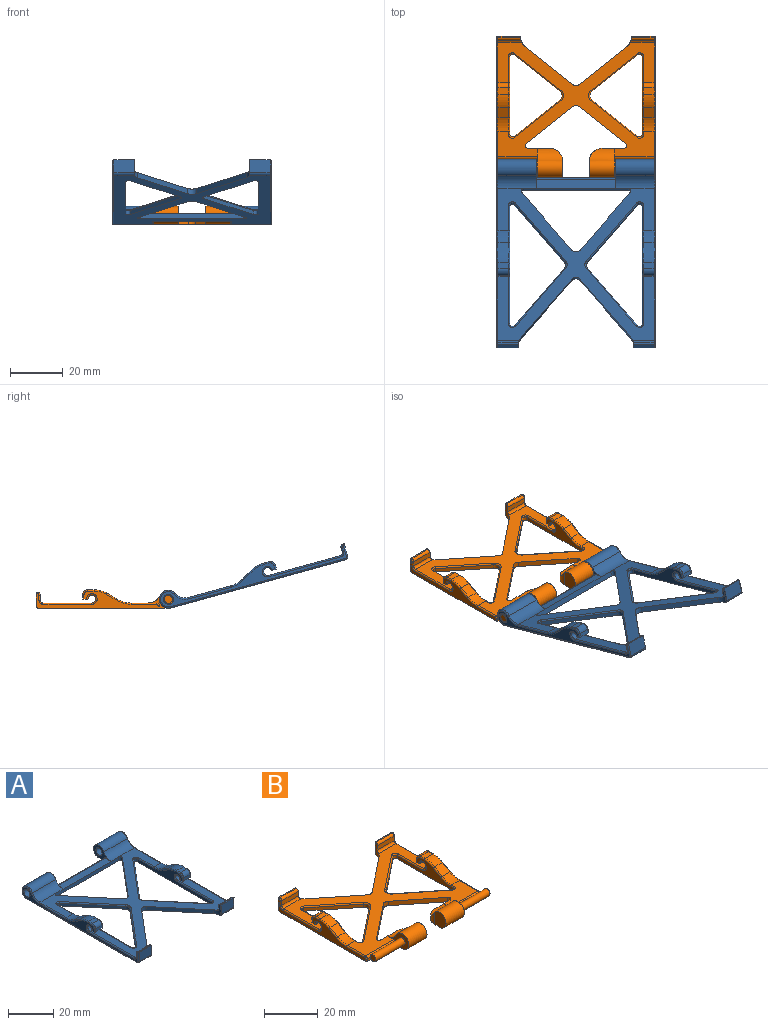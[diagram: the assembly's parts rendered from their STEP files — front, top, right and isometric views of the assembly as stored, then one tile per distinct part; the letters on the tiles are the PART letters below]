
ASSEMBLY  parts=2 mates=1
PART A: 132 faces, bbox 60x73.4x8.1 mm
  f0: plane 68.6x59mm, normal (0,0,-1), area 1652.7mm2, adj f4,f10,f14,f16,f19,f23,f25,f33
  f1: plane 7.77x5mm, normal (0,-1,0), area 38.8mm2, adj f3,f4,f55,f113
  f2: plane 7.83x2mm, normal (0,1,0), area 15.7mm2, adj f5,f6,f57,f107
  f3: plane 7.77x0.5mm, normal (0,0,1), area 3.9mm2, adj f1,f5,f55,f111
  f4: cylinder r=1mm len=7.78mm, axis (1,0,0), area 12.2mm2, adj f0,f1,f55,f57,f112
  f5: cylinder r=1mm len=7.83mm, axis (1,0,0), area 12.2mm2, adj f2,f3,f55,f57,f109
  f6: cylinder r=1mm len=8.11mm, axis (-1,0,0), area 12.4mm2, adj f2,f8,f57,f105
  f7: plane 30x3.49mm, normal (0,0,1), area 104.7mm2, adj f16,f18,f25,f48
  f8: plane 59.51x59mm, normal (0,0,1), area 1041.3mm2, adj f6,f17,f21,f26,f27,f34,f43,f44
  f9: plane 72x6mm, normal (-1,0,0), area 126.8mm2, adj f15,f32,f96,f97,f98,f99,f100,f101
  f10: plane 30x1mm, normal (0,1,0), area 30mm2, adj f0,f16,f18,f25
  f11: plane 7.83x2mm, normal (0,1,0), area 15.7mm2, adj f20,f21,f56,f125
  f12: plane 7.77x5mm, normal (0,-1,0), area 38.8mm2, adj f13,f19,f54,f131
  f13: plane 7.77x0.5mm, normal (0,0,1), area 3.9mm2, adj f12,f20,f54,f129
  f14: cylinder r=3.4mm len=14.5mm, axis (-1,0,0), area 210.5mm2, adj f0,f16,f17,f108
  f15: cylinder r=1.9mm len=15mm, axis (-1,0,0), area 179.1mm2, adj f9,f16
  f16: plane 10.99x6.8mm, normal (1,0,0), area 29.9mm2, adj f0,f7,f10,f14,f15,f17,f18
  f17: cylinder r=5mm len=14.5mm, axis (-1,0,0), area 81.8mm2, adj f8,f14,f16,f48,f106
  f18: cylinder r=1mm len=30mm, axis (1,0,0), area 47.1mm2, adj f7,f10,f16,f25
  f19: cylinder r=1mm len=7.78mm, axis (1,0,0), area 12.2mm2, adj f0,f12,f54,f56,f130
  f20: cylinder r=1mm len=7.83mm, axis (1,0,0), area 12.2mm2, adj f11,f13,f54,f56,f127
  f21: cylinder r=1mm len=8.11mm, axis (-1,0,0), area 12.4mm2, adj f8,f11,f56,f123
  f22: plane 72x6mm, normal (1,0,0), area 126.8mm2, adj f24,f39,f114,f115,f116,f117,f118,f119
  f23: cylinder r=3.4mm len=14.5mm, axis (1,0,0), area 210.5mm2, adj f0,f25,f26,f126
  f24: cylinder r=1.9mm len=15mm, axis (1,0,0), area 179.1mm2, adj f22,f25
  f25: plane 10.99x6.8mm, normal (-1,0,0), area 29.9mm2, adj f0,f7,f10,f18,f23,f24,f26
  f26: cylinder r=5mm len=14.5mm, axis (1,0,0), area 81.8mm2, adj f8,f23,f25,f48,f124
  f27: cylinder r=1.5mm len=4mm, axis (-1,0,0), area 28.3mm2, adj f8,f32,f82,f101
  f28: plane 4.02x4mm, normal (0,0.5,0.87), area 18.6mm2, adj f52,f53,f91,f100
  f29: plane 4x2.32mm, normal (0,0,1), area 9.3mm2, adj f30,f53,f93,f98
  f30: cylinder r=2mm len=4mm, axis (-1,0,0), area 12.6mm2, adj f29,f31,f94,f97
  f31: plane 4x1.5mm, normal (0,-1,0), area 6mm2, adj f30,f32,f95,f96
  f32: plane 5x2mm, normal (0,0,-1), area 9.8mm2, adj f9,f27,f31,f33,f82,f95,f96,f101
  f33: plane 46.25x6.5mm, normal (1,0,0), area 107.1mm2, adj f0,f32,f66,f67,f82,f83,f89,f90
  f34: cylinder r=1.5mm len=4mm, axis (1,0,0), area 28.3mm2, adj f8,f39,f68,f119
  f35: plane 4.02x4mm, normal (0,0.5,0.87), area 18.6mm2, adj f50,f51,f77,f118
  f36: plane 4x2.32mm, normal (0,0,1), area 9.3mm2, adj f37,f51,f79,f116
  f37: cylinder r=2mm len=4mm, axis (1,0,0), area 12.6mm2, adj f36,f38,f80,f115
  f38: plane 4x1.5mm, normal (0,-1,0), area 6mm2, adj f37,f39,f81,f114
  f39: plane 5x2mm, normal (0,0,-1), area 9.8mm2, adj f22,f34,f38,f40,f68,f81,f114,f119
  f40: plane 46.25x6.5mm, normal (-1,0,0), area 107.1mm2, adj f0,f39,f64,f65,f68,f69,f75,f76
  f41: plane 22.48x18.89mm, normal (-0.77,0.64,0), area 44mm2, adj f0,f61,f67,f85
  f42: plane 22.48x18.89mm, normal (-0.77,-0.64,0), area 44mm2, adj f0,f61,f66,f87
  f43: plane 22.65x19.03mm, normal (-0.77,-0.64,0), area 59.2mm2, adj f0,f8,f56,f58
  f44: plane 22.65x19.03mm, normal (0.77,-0.64,0), area 59.2mm2, adj f0,f8,f57,f58
  f45: plane 22.48x18.89mm, normal (0.77,-0.64,0), area 44mm2, adj f0,f60,f64,f73
  f46: plane 22.48x18.89mm, normal (0.77,0.64,0), area 44mm2, adj f0,f60,f65,f71
  f47: plane 22.4x18.82mm, normal (0.77,0.64,0), area 58.5mm2, adj f0,f8,f59,f63
  f48: plane 39.18x2mm, normal (0,-1,0), area 78.4mm2, adj f0,f7,f17,f26,f62,f63
  f49: plane 22.4x18.82mm, normal (-0.77,0.64,0), area 58.5mm2, adj f0,f8,f59,f62
  f50: cylinder r=10mm len=5mm, axis (-1,0,0), area 20.9mm2, adj f8,f35,f76,f120
  f51: cylinder r=10mm len=5mm, axis (1,0,0), area 20.9mm2, adj f35,f36,f78,f117
  f52: cylinder r=10mm len=5mm, axis (1,0,0), area 20.9mm2, adj f8,f28,f90,f102
  f53: cylinder r=10mm len=5mm, axis (-1,0,0), area 20.9mm2, adj f28,f29,f92,f99
  f54: plane 5.95x0.68mm, normal (-1,0,0), area 3.9mm2, adj f12,f13,f19,f20,f56
  f55: plane 5.95x0.68mm, normal (1,0,0), area 3.9mm2, adj f1,f3,f4,f5,f57
  f56: cylinder r=5mm len=5.98mm, axis (0,0,1), area 10.3mm2, adj f0,f8,f11,f19,f20,f21,f43,f54
  f57: cylinder r=5mm len=5.98mm, axis (0,0,-1), area 10.3mm2, adj f0,f2,f4,f5,f6,f8,f44,f55
  f58: cylinder r=2mm len=3.06mm, axis (0,0,-1), area 7mm2, adj f0,f8,f43,f44
  f59: cylinder r=2mm len=3.06mm, axis (0,0,1), area 7mm2, adj f0,f8,f47,f49
  f60: cylinder r=2mm len=2.57mm, axis (0,0,-1), area 4.2mm2, adj f0,f45,f46,f72
  f61: cylinder r=2mm len=2.57mm, axis (0,0,-1), area 4.2mm2, adj f0,f41,f42,f86
  f62: cylinder r=1mm len=2mm, axis (0,0,1), area 4.5mm2, adj f0,f8,f48,f49
  f63: cylinder r=1mm len=2mm, axis (0,0,-1), area 4.5mm2, adj f0,f8,f47,f48
  f64: cylinder r=1mm len=1.77mm, axis (0,0,1), area 3.7mm2, adj f0,f40,f45,f74
  f65: cylinder r=1mm len=1.77mm, axis (0,0,1), area 3.7mm2, adj f0,f40,f46,f70
  f66: cylinder r=1mm len=1.77mm, axis (0,0,-1), area 3.7mm2, adj f0,f33,f42,f88
  f67: cylinder r=1mm len=1.77mm, axis (0,0,-1), area 3.7mm2, adj f0,f33,f41,f84
  f68: torus R=2mm, axis (1,0,0), area 6.2mm2, adj f34,f39,f40,f69
  f69: cylinder r=0.5mm len=21.57mm, axis (0,1,0), area 16.9mm2, adj f8,f40,f68,f70
  f70: torus R=1.5mm, axis (0,0,1), area 2.3mm2, adj f8,f65,f69,f71
  f71: cylinder r=0.5mm len=22.8mm, axis (-0.64,0.77,0), area 23.1mm2, adj f8,f46,f70,f72
  f72: torus R=2.5mm, axis (0,0,1), area 2.4mm2, adj f8,f60,f71,f73
  f73: cylinder r=0.5mm len=22.8mm, axis (0.64,0.77,0), area 23.1mm2, adj f8,f45,f72,f74
  f74: torus R=1.5mm, axis (0,0,1), area 2.3mm2, adj f8,f64,f73,f75
  f75: cylinder r=0.5mm len=9.84mm, axis (0,1,0), area 7.7mm2, adj f8,f40,f74,f76
  f76: torus R=10.5mm, axis (1,0,0), area 4.2mm2, adj f40,f50,f75,f77
  f77: cylinder r=0.5mm len=4.27mm, axis (0,0.87,-0.5), area 3.6mm2, adj f35,f40,f76,f78
  f78: torus R=9.5mm, axis (1,0,0), area 4mm2, adj f40,f51,f77,f79
  f79: cylinder r=0.5mm len=2.32mm, axis (0,1,0), area 1.8mm2, adj f36,f40,f78,f80
  f80: torus R=1.5mm, axis (1,0,0), area 2.2mm2, adj f37,f40,f79,f81
  f81: cylinder r=0.5mm len=1.5mm, axis (0,0,1), area 1.2mm2, adj f38,f39,f40,f80
  f82: torus R=2mm, axis (-1,0,0), area 6.2mm2, adj f27,f32,f33,f83
  f83: cylinder r=0.5mm len=21.57mm, axis (0,-1,0), area 16.9mm2, adj f8,f33,f82,f84
  f84: torus R=1.5mm, axis (0,0,1), area 2.3mm2, adj f8,f67,f83,f85
  f85: cylinder r=0.5mm len=22.8mm, axis (-0.64,-0.77,0), area 23.1mm2, adj f8,f41,f84,f86
  f86: torus R=2.5mm, axis (0,0,1), area 2.4mm2, adj f8,f61,f85,f87
  f87: cylinder r=0.5mm len=22.8mm, axis (0.64,-0.77,0), area 23.1mm2, adj f8,f42,f86,f88
  f88: torus R=1.5mm, axis (0,0,1), area 2.3mm2, adj f8,f66,f87,f89
  f89: cylinder r=0.5mm len=9.84mm, axis (0,-1,0), area 7.7mm2, adj f8,f33,f88,f90
  f90: torus R=10.5mm, axis (-1,0,0), area 4.2mm2, adj f33,f52,f89,f91
  f91: cylinder r=0.5mm len=4.27mm, axis (0,0.87,-0.5), area 3.6mm2, adj f28,f33,f90,f92
  f92: torus R=9.5mm, axis (-1,0,0), area 4mm2, adj f33,f53,f91,f93
  f93: cylinder r=0.5mm len=2.32mm, axis (0,1,0), area 1.8mm2, adj f29,f33,f92,f94
  f94: torus R=1.5mm, axis (-1,0,0), area 2.2mm2, adj f30,f33,f93,f95
  f95: cylinder r=0.5mm len=1.5mm, axis (0,0,1), area 1.2mm2, adj f31,f32,f33,f94
  f96: cylinder r=0.5mm len=1.5mm, axis (0,0,1), area 1.2mm2, adj f9,f31,f32,f97
  f97: torus R=1.5mm, axis (1,0,0), area 2.2mm2, adj f9,f30,f96,f98
  f98: cylinder r=0.5mm len=2.32mm, axis (0,1,0), area 1.8mm2, adj f9,f29,f97,f99
  f99: torus R=9.5mm, axis (1,0,0), area 4mm2, adj f9,f53,f98,f100
  f100: cylinder r=0.5mm len=4.27mm, axis (0,0.87,-0.5), area 3.6mm2, adj f9,f28,f99,f102
  f101: torus R=2mm, axis (1,0,0), area 6.2mm2, adj f9,f27,f32,f103
  f102: torus R=10.5mm, axis (1,0,0), area 4.2mm2, adj f9,f52,f100,f104
  f103: cylinder r=0.5mm len=28.2mm, axis (0,1,0), area 22.1mm2, adj f8,f9,f101,f105
  f104: cylinder r=0.5mm len=16.47mm, axis (0,1,0), area 12.9mm2, adj f8,f9,f102,f106
  f105: torus R=1.5mm, axis (1,0,0), area 1.5mm2, adj f6,f9,f103,f107
  f106: torus R=5.5mm, axis (1,0,0), area 4.6mm2, adj f9,f17,f104,f108
  f107: cylinder r=0.5mm len=2mm, axis (0,0,1), area 1.6mm2, adj f2,f9,f105,f109
  f108: torus R=2.9mm, axis (1,0,0), area 10.8mm2, adj f9,f14,f106,f110
  f109: torus R=0.5mm, axis (1,0,0), area 1mm2, adj f5,f9,f107,f111
  f110: cylinder r=0.5mm len=68.6mm, axis (0,-1,0), area 53.9mm2, adj f0,f9,f108,f112
  f111: cylinder r=0.5mm len=0.5mm, axis (0,1,0), area 0.2mm2, adj f3,f109,f113
  f112: torus R=0.5mm, axis (1,0,0), area 1mm2, adj f4,f9,f110,f113
  f113: cylinder r=0.5mm len=5mm, axis (0,0,-1), area 3.8mm2, adj f1,f9,f111,f112
  f114: cylinder r=0.5mm len=1.5mm, axis (0,0,1), area 1.2mm2, adj f22,f38,f39,f115
  f115: torus R=1.5mm, axis (-1,0,0), area 2.2mm2, adj f22,f37,f114,f116
  f116: cylinder r=0.5mm len=2.32mm, axis (0,1,0), area 1.8mm2, adj f22,f36,f115,f117
  f117: torus R=9.5mm, axis (-1,0,0), area 4mm2, adj f22,f51,f116,f118
  f118: cylinder r=0.5mm len=4.27mm, axis (0,0.87,-0.5), area 3.6mm2, adj f22,f35,f117,f120
  f119: torus R=2mm, axis (-1,0,0), area 6.2mm2, adj f22,f34,f39,f121
  f120: torus R=10.5mm, axis (-1,0,0), area 4.2mm2, adj f22,f50,f118,f122
  f121: cylinder r=0.5mm len=28.2mm, axis (0,1,0), area 22.1mm2, adj f8,f22,f119,f123
  f122: cylinder r=0.5mm len=16.47mm, axis (0,1,0), area 12.9mm2, adj f8,f22,f120,f124
  f123: torus R=1.5mm, axis (-1,0,0), area 1.5mm2, adj f21,f22,f121,f125
  f124: torus R=5.5mm, axis (-1,0,0), area 4.6mm2, adj f22,f26,f122,f126
  f125: cylinder r=0.5mm len=2mm, axis (0,0,1), area 1.6mm2, adj f11,f22,f123,f127
  f126: torus R=2.9mm, axis (-1,0,0), area 10.8mm2, adj f22,f23,f124,f128
  f127: torus R=0.5mm, axis (-1,0,0), area 1mm2, adj f20,f22,f125,f129
  f128: cylinder r=0.5mm len=68.6mm, axis (0,-1,0), area 53.9mm2, adj f0,f22,f126,f130
  f129: cylinder r=0.5mm len=0.5mm, axis (0,1,0), area 0.3mm2, adj f13,f127,f131
  f130: torus R=0.5mm, axis (-1,0,0), area 1mm2, adj f19,f22,f128,f131
  f131: cylinder r=0.5mm len=5mm, axis (0,0,-1), area 3.8mm2, adj f12,f22,f129,f130
PART B: 134 faces, bbox 60x53.3x7.8 mm
  f0: plane 60x48.9mm, normal (0,0,-1), area 1289.4mm2, adj f2,f6,f9,f10,f14,f15,f16,f21
  f1: plane 9.01x5mm, normal (0,1,0), area 45mm2, adj f4,f6,f32,f60,f118
  f2: plane 8.13x2mm, normal (0,1,0), area 16.3mm2, adj f0,f8,f33,f62,f71
  f3: plane 8.72x2mm, normal (0,-1,0), area 17.4mm2, adj f5,f7,f64,f116
  f4: plane 8.53x0.5mm, normal (0,0,1), area 4.3mm2, adj f1,f5,f60,f64,f118
  f5: cylinder r=1mm len=8.72mm, axis (-1,0,0), area 13.5mm2, adj f3,f4,f64,f117
  f6: cylinder r=1mm len=9.1mm, axis (-1,0,0), area 14.2mm2, adj f0,f1,f32,f60,f64
  f7: cylinder r=1mm len=9.13mm, axis (1,0,0), area 13.9mm2, adj f3,f8,f64,f115
  f8: plane 59x43mm, normal (0,0,1), area 850.6mm2, adj f2,f7,f14,f22,f23,f24,f36,f39
  f9: plane 14.9x1mm, normal (0,-1,0), area 14.9mm2, adj f0,f14,f22,f112
  f10: plane 46x6.5mm, normal (-1,0,0), area 110.9mm2, adj f0,f19,f21,f29,f104,f105,f106,f107
  f11: cylinder r=5mm len=9.58mm, axis (-1,0,0), area 48.5mm2, adj f14,f15,f55,f63
  f12: cylinder r=1.5mm len=15.4mm, axis (-1,0,0), area 145.1mm2, adj f13,f14
  f13: plane 3x3mm, normal (-1,0,0), area 7.1mm2, adj f12
  f14: plane 10.99x6.8mm, normal (-1,0,0), area 34.8mm2, adj f0,f8,f9,f11,f12,f15,f22
  f15: cylinder r=3.4mm len=9.6mm, axis (-1,0,0), area 139.3mm2, adj f0,f11,f14,f16,f63
  f16: plane 6.8x5.99mm, normal (1,0,0), area 34.8mm2, adj f0,f15,f63
  f17: plane 8.72x2mm, normal (0,-1,0), area 17.4mm2, adj f20,f23,f65,f131
  f18: plane 8.53x0.5mm, normal (0,0,1), area 4.3mm2, adj f19,f20,f61,f65,f133
  f19: plane 9.01x5mm, normal (0,1,0), area 45mm2, adj f10,f18,f21,f61,f133
  f20: cylinder r=1mm len=8.72mm, axis (-1,0,0), area 13.5mm2, adj f17,f18,f65,f132
  f21: cylinder r=1mm len=9.1mm, axis (-1,0,0), area 14.2mm2, adj f0,f10,f19,f61,f65
  f22: cylinder r=1mm len=14.9mm, axis (-1,0,0), area 23.4mm2, adj f8,f9,f14,f111
  f23: cylinder r=1mm len=9.13mm, axis (1,0,0), area 13.9mm2, adj f8,f17,f65,f130
  f24: cylinder r=1.5mm len=4mm, axis (-1,0,0), area 28.3mm2, adj f8,f29,f76,f128
  f25: plane 4.02x4mm, normal (0,-0.5,0.87), area 18.6mm2, adj f58,f59,f85,f108
  f26: plane 4x2.32mm, normal (0,0,1), area 9.3mm2, adj f27,f59,f87,f106
  f27: cylinder r=2mm len=4mm, axis (-1,0,0), area 12.6mm2, adj f26,f28,f88,f105
  f28: plane 4x1.5mm, normal (0,1,0), area 6mm2, adj f27,f29,f89,f104
  f29: plane 5x2mm, normal (0,0,-1), area 9.8mm2, adj f10,f24,f28,f30,f76,f89,f104,f128
  f30: plane 29.27x6.5mm, normal (1,0,0), area 81.6mm2, adj f0,f29,f74,f75,f76,f77,f83,f84
  f31: plane 14.9x1mm, normal (0,-1,0), area 14.9mm2, adj f0,f36,f39,f127
  f32: plane 46x6.5mm, normal (1,0,0), area 110.9mm2, adj f0,f1,f6,f45,f113,f114,f115,f116
  f33: cylinder r=5mm len=9.58mm, axis (1,0,0), area 48.5mm2, adj f2,f36,f37,f62
  f34: cylinder r=1.5mm len=15.4mm, axis (1,0,0), area 145.1mm2, adj f35,f36
  f35: plane 3x3mm, normal (1,0,0), area 7.1mm2, adj f34
  f36: plane 10.99x6.8mm, normal (1,0,0), area 34.8mm2, adj f0,f8,f31,f33,f34,f37,f39
  f37: cylinder r=3.4mm len=9.6mm, axis (1,0,0), area 139.3mm2, adj f0,f33,f36,f38,f62
  f38: plane 6.8x5.99mm, normal (-1,0,0), area 34.8mm2, adj f0,f37,f62
  f39: cylinder r=1mm len=14.9mm, axis (1,0,0), area 23.4mm2, adj f8,f31,f36,f126
  f40: cylinder r=1.5mm len=4mm, axis (1,0,0), area 28.3mm2, adj f8,f45,f90,f113
  f41: plane 4.02x4mm, normal (0,-0.5,0.87), area 18.6mm2, adj f56,f57,f99,f123
  f42: plane 4x2.32mm, normal (0,0,1), area 9.3mm2, adj f43,f56,f101,f121
  f43: cylinder r=2mm len=4mm, axis (1,0,0), area 12.6mm2, adj f42,f44,f102,f120
  f44: plane 4x1.5mm, normal (0,1,0), area 6mm2, adj f43,f45,f103,f119
  f45: plane 5x2mm, normal (0,0,-1), area 9.8mm2, adj f32,f40,f44,f46,f90,f103,f113,f119
  f46: plane 29.27x6.5mm, normal (-1,0,0), area 81.6mm2, adj f0,f45,f72,f73,f90,f91,f97,f98
  f47: plane 17.4x13.85mm, normal (-0.62,-0.78,0), area 33.4mm2, adj f0,f69,f75,f79
  f48: plane 17.4x13.85mm, normal (-0.62,0.78,0), area 33.4mm2, adj f0,f69,f74,f81
  f49: plane 17.86x14.22mm, normal (0.62,0.78,0), area 45.6mm2, adj f0,f8,f65,f66
  f50: plane 17.86x14.22mm, normal (-0.62,0.78,0), area 45.6mm2, adj f0,f8,f64,f66
  f51: plane 17.4x13.85mm, normal (0.62,0.78,0), area 33.4mm2, adj f0,f68,f72,f95
  f52: plane 17.4x13.85mm, normal (0.62,-0.78,0), area 33.4mm2, adj f0,f68,f73,f93
  f53: plane 17.5x13.94mm, normal (-0.62,-0.78,0), area 44.7mm2, adj f0,f8,f67,f71
  f54: plane 17.5x13.94mm, normal (0.62,-0.78,0), area 44.7mm2, adj f0,f8,f67,f70
  f55: plane 8.13x2mm, normal (0,1,0), area 16.3mm2, adj f0,f8,f11,f63,f70
  f56: cylinder r=10mm len=5mm, axis (1,0,0), area 20.9mm2, adj f41,f42,f100,f122
  f57: cylinder r=10mm len=5mm, axis (-1,0,0), area 20.9mm2, adj f8,f41,f98,f124
  f58: cylinder r=10mm len=5mm, axis (1,0,0), area 20.9mm2, adj f8,f25,f84,f109
  f59: cylinder r=10mm len=5mm, axis (-1,0,0), area 20.9mm2, adj f25,f26,f86,f107
  f60: plane 5.41x0.09mm, normal (-1,0,0), area 0.5mm2, adj f1,f4,f6,f64
  f61: plane 5.41x0.09mm, normal (1,0,0), area 0.5mm2, adj f18,f19,f21,f65
  f62: cylinder r=5mm len=5.6mm, axis (0,0,-1), area 21.2mm2, adj f0,f2,f33,f37,f38
  f63: cylinder r=5mm len=5.6mm, axis (0,0,-1), area 21.2mm2, adj f0,f11,f15,f16,f55
  f64: cylinder r=5mm len=6mm, axis (0,0,1), area 14.6mm2, adj f0,f3,f4,f5,f6,f7,f8,f50
  f65: cylinder r=5mm len=6mm, axis (0,0,-1), area 14.6mm2, adj f0,f8,f17,f18,f20,f21,f23,f49
  f66: cylinder r=2mm len=2.49mm, axis (0,0,-1), area 5.4mm2, adj f0,f8,f49,f50
  f67: cylinder r=2mm len=2.49mm, axis (0,0,-1), area 5.4mm2, adj f0,f8,f53,f54
  f68: cylinder r=2mm len=3.13mm, axis (0,0,1), area 5.4mm2, adj f0,f51,f52,f94
  f69: cylinder r=2mm len=3.13mm, axis (0,0,-1), area 5.4mm2, adj f0,f47,f48,f80
  f70: cylinder r=1mm len=2mm, axis (0,0,1), area 4.9mm2, adj f0,f8,f54,f55
  f71: cylinder r=1mm len=2mm, axis (0,0,1), area 4.9mm2, adj f0,f2,f8,f53
  f72: cylinder r=1mm len=1.62mm, axis (0,0,-1), area 3.4mm2, adj f0,f46,f51,f96
  f73: cylinder r=1mm len=1.62mm, axis (0,0,1), area 3.4mm2, adj f0,f46,f52,f92
  f74: cylinder r=1mm len=1.62mm, axis (0,0,-1), area 3.4mm2, adj f0,f30,f48,f82
  f75: cylinder r=1mm len=1.62mm, axis (0,0,-1), area 3.4mm2, adj f0,f30,f47,f78
  f76: torus R=2mm, axis (-1,0,0), area 6.2mm2, adj f24,f29,f30,f77
  f77: cylinder r=0.5mm len=13.23mm, axis (0,1,0), area 10.4mm2, adj f8,f30,f76,f78
  f78: torus R=1.5mm, axis (0,0,1), area 2.1mm2, adj f8,f75,f77,f79
  f79: cylinder r=0.5mm len=17.71mm, axis (0.78,-0.62,0), area 17.5mm2, adj f8,f47,f78,f80
  f80: torus R=2.5mm, axis (0,0,1), area 3.1mm2, adj f8,f69,f79,f81
  f81: cylinder r=0.5mm len=17.71mm, axis (-0.78,-0.62,0), area 17.5mm2, adj f8,f48,f80,f82
  f82: torus R=1.5mm, axis (0,0,1), area 2.1mm2, adj f8,f74,f81,f83
  f83: cylinder r=0.5mm len=1.2mm, axis (0,1,0), area 0.9mm2, adj f8,f30,f82,f84
  f84: torus R=10.5mm, axis (-1,0,0), area 4.2mm2, adj f30,f58,f83,f85
  f85: cylinder r=0.5mm len=4.27mm, axis (0,-0.87,-0.5), area 3.6mm2, adj f25,f30,f84,f86
  f86: torus R=9.5mm, axis (-1,0,0), area 4mm2, adj f30,f59,f85,f87
  f87: cylinder r=0.5mm len=2.32mm, axis (0,-1,0), area 1.8mm2, adj f26,f30,f86,f88
  f88: torus R=1.5mm, axis (-1,0,0), area 2.2mm2, adj f27,f30,f87,f89
  f89: cylinder r=0.5mm len=1.5mm, axis (0,0,1), area 1.2mm2, adj f28,f29,f30,f88
  f90: torus R=2mm, axis (1,0,0), area 6.2mm2, adj f40,f45,f46,f91
  f91: cylinder r=0.5mm len=13.23mm, axis (0,-1,0), area 10.4mm2, adj f8,f46,f90,f92
  f92: torus R=1.5mm, axis (0,0,1), area 2.1mm2, adj f8,f73,f91,f93
  f93: cylinder r=0.5mm len=17.71mm, axis (0.78,0.62,0), area 17.5mm2, adj f8,f52,f92,f94
  f94: torus R=2.5mm, axis (0,0,1), area 3.1mm2, adj f8,f68,f93,f95
  f95: cylinder r=0.5mm len=17.71mm, axis (-0.78,0.62,0), area 17.5mm2, adj f8,f51,f94,f96
  f96: torus R=1.5mm, axis (0,0,1), area 2.1mm2, adj f8,f72,f95,f97
  f97: cylinder r=0.5mm len=1.2mm, axis (0,-1,0), area 0.9mm2, adj f8,f46,f96,f98
  f98: torus R=10.5mm, axis (1,0,0), area 4.2mm2, adj f46,f57,f97,f99
  f99: cylinder r=0.5mm len=4.27mm, axis (0,-0.87,-0.5), area 3.6mm2, adj f41,f46,f98,f100
  f100: torus R=9.5mm, axis (1,0,0), area 4mm2, adj f46,f56,f99,f101
  f101: cylinder r=0.5mm len=2.32mm, axis (0,-1,0), area 1.8mm2, adj f42,f46,f100,f102
  f102: torus R=1.5mm, axis (1,0,0), area 2.2mm2, adj f43,f46,f101,f103
  f103: cylinder r=0.5mm len=1.5mm, axis (0,0,1), area 1.2mm2, adj f44,f45,f46,f102
  f104: cylinder r=0.5mm len=1.5mm, axis (0,0,-1), area 1.2mm2, adj f10,f28,f29,f105
  f105: torus R=1.5mm, axis (-1,0,0), area 2.2mm2, adj f10,f27,f104,f106
  f106: cylinder r=0.5mm len=2.32mm, axis (0,1,0), area 1.8mm2, adj f10,f26,f105,f107
  f107: torus R=9.5mm, axis (-1,0,0), area 4mm2, adj f10,f59,f106,f108
  f108: cylinder r=0.5mm len=4.27mm, axis (0,0.87,0.5), area 3.6mm2, adj f10,f25,f107,f109
  f109: torus R=10.5mm, axis (-1,0,0), area 4.2mm2, adj f10,f58,f108,f110
  f110: cylinder r=0.5mm len=9.66mm, axis (0,1,0), area 7.6mm2, adj f8,f10,f109,f111
  f111: torus R=0.5mm, axis (-1,0,0), area 1mm2, adj f10,f22,f110,f112
  f112: cylinder r=0.5mm len=1mm, axis (0,0,-1), area 0.8mm2, adj f0,f9,f10,f111
  f113: torus R=2mm, axis (1,0,0), area 6.2mm2, adj f32,f40,f45,f114
  f114: cylinder r=0.5mm len=18.5mm, axis (0,1,0), area 14.5mm2, adj f8,f32,f113,f115
  f115: torus R=1.5mm, axis (1,0,0), area 1.5mm2, adj f7,f32,f114,f116
  f116: cylinder r=0.5mm len=2mm, axis (0,0,-1), area 1.6mm2, adj f3,f32,f115,f117
  f117: torus R=0.5mm, axis (1,0,0), area 1mm2, adj f5,f32,f116,f118
  f118: cylinder r=0.5mm len=0.5mm, axis (0,1,0), area 0.4mm2, adj f1,f4,f32,f117
  f119: cylinder r=0.5mm len=1.5mm, axis (0,0,-1), area 1.2mm2, adj f32,f44,f45,f120
  f120: torus R=1.5mm, axis (1,0,0), area 2.2mm2, adj f32,f43,f119,f121
  f121: cylinder r=0.5mm len=2.32mm, axis (0,1,0), area 1.8mm2, adj f32,f42,f120,f122
  f122: torus R=9.5mm, axis (1,0,0), area 4mm2, adj f32,f56,f121,f123
  f123: cylinder r=0.5mm len=4.27mm, axis (0,0.87,0.5), area 3.6mm2, adj f32,f41,f122,f124
  f124: torus R=10.5mm, axis (1,0,0), area 4.2mm2, adj f32,f57,f123,f125
  f125: cylinder r=0.5mm len=9.66mm, axis (0,1,0), area 7.6mm2, adj f8,f32,f124,f126
  f126: torus R=0.5mm, axis (1,0,0), area 1mm2, adj f32,f39,f125,f127
  f127: cylinder r=0.5mm len=1mm, axis (0,0,-1), area 0.8mm2, adj f0,f31,f32,f126
  f128: torus R=2mm, axis (-1,0,0), area 6.2mm2, adj f10,f24,f29,f129
  f129: cylinder r=0.5mm len=18.5mm, axis (0,1,0), area 14.5mm2, adj f8,f10,f128,f130
  f130: torus R=1.5mm, axis (-1,0,0), area 1.5mm2, adj f10,f23,f129,f131
  f131: cylinder r=0.5mm len=2mm, axis (0,0,-1), area 1.6mm2, adj f10,f17,f130,f132
  f132: torus R=0.5mm, axis (-1,0,0), area 1mm2, adj f10,f20,f131,f133
  f133: cylinder r=0.5mm len=0.5mm, axis (0,1,0), area 0.4mm2, adj f10,f18,f19,f132
PLACE A rot(axis=(-1,0,0),15.4deg) t=(0,-27.09,0.95)mm
PLACE B t=(0,-26.3,0)mm
MATE revolute A.f23 <-> B.f37  axis (1,0,0) through (30,-23.2,3.4)mm
